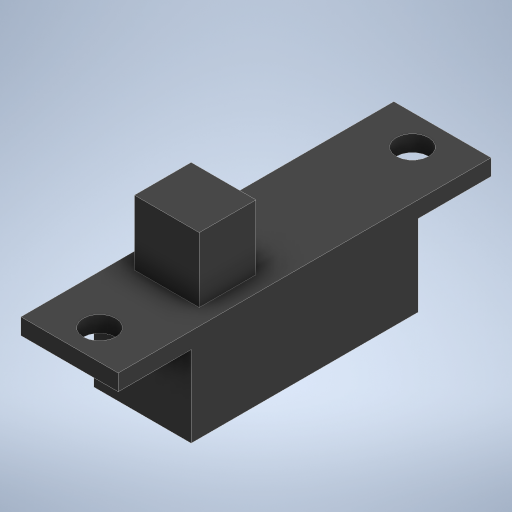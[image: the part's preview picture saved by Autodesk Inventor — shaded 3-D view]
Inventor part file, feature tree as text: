
AUTODESK INVENTOR PART (.ipt)
format: ipt  version: 2024.2 (Build 282272000, 272)  size: 249,856 bytes
history: native  units: mm
features: extrude x3, sketch x3
ambient origin geometry x8: Origin, YZ Plane, XZ Plane, XY Plane, X Axis, Y Axis, Z Axis, Center Point
bodies: Solid1 (feature_tree)
feature tree (6):
  extrude  "Extrusion1"  Depth=23.0mm
  extrude  "Extrusion2"  Depth=2.0mm
  extrude  "Extrusion3"  Depth=4.0mm
  sketch  "Sketch1"  dims[d0=6.0mm d1=23.0mm]
  sketch  "Sketch2"  dims[d2=2.0mm d3=2.0mm]
  sketch  "Sketch3"  dims[d4=19.3mm d5=1.85mm d6=3.0mm d7=1.0mm d8=0.0mm d9=14.0mm d10=4.5mm d11=5.0mm d12=0.0mm d13=4.0mm d14=3.5mm d15=1.0mm d16=6.0mm d17=4.0mm d18=0.0mm]
